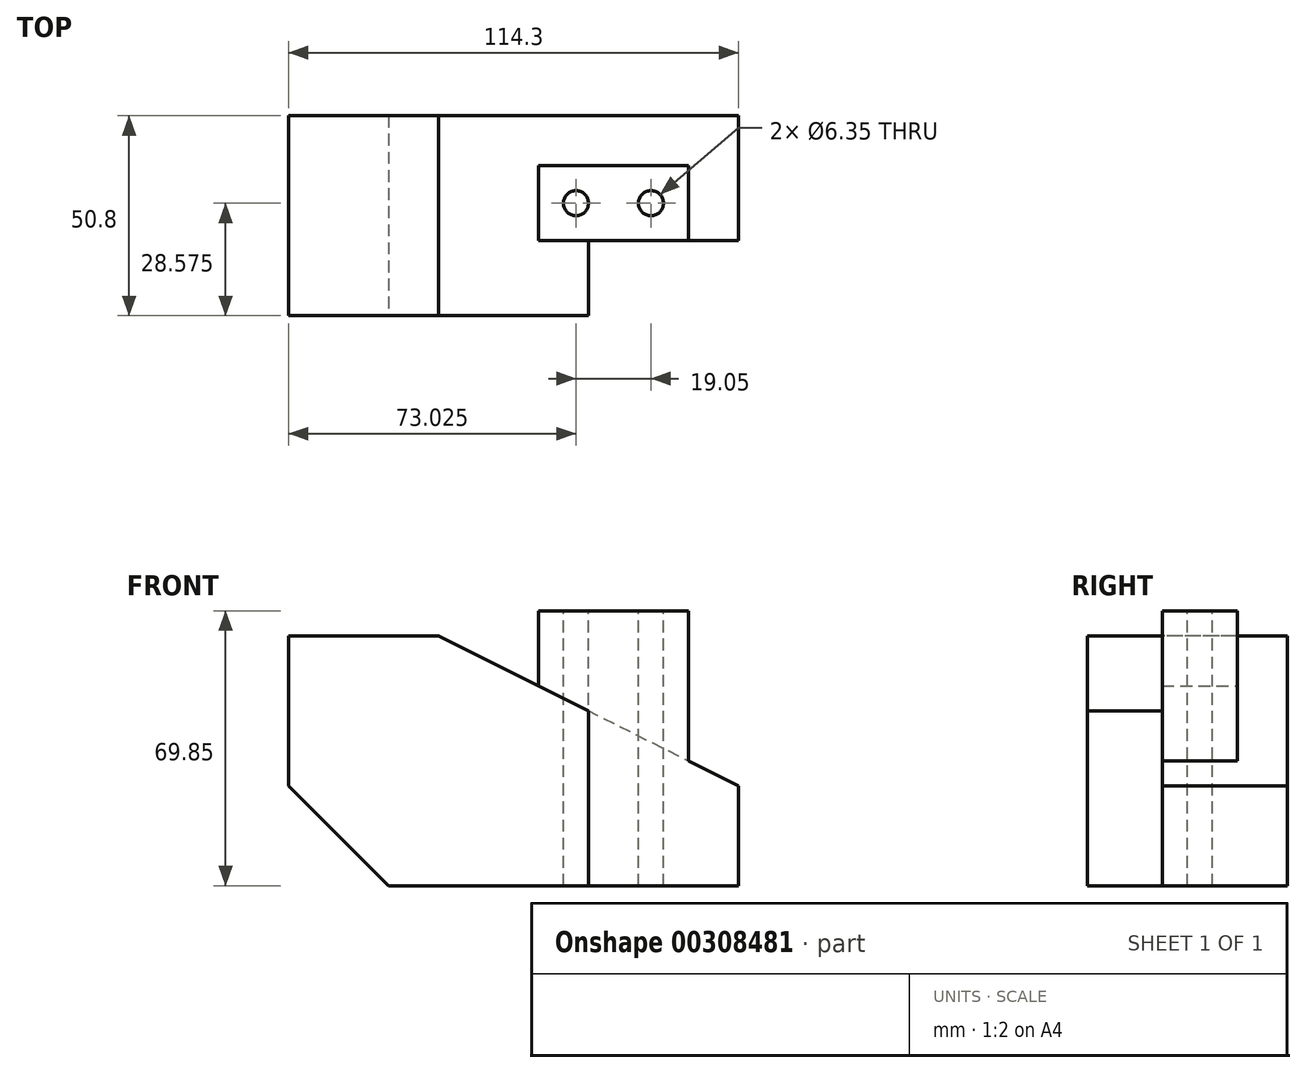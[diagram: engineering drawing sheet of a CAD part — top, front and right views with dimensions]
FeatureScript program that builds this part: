
annotation { "Feature Type Name" : "Feature", "Feature Type Description" : "" }
export const myFeature = defineFeature(function(context is Context, id is Id, definition is map)
    precondition{}
    {
        {
            var Q0;
            Q0=qCreatedBy(makeId("Front.planeOp"),FACE);
            var sketch = newSketch(context, id + "F0", { "sketchPlane" : qUnion([Q0])});
            skLineSegment(sketch, "E0", {"start": v(0, 0) * mm, "end": v(0, 38.1) * mm});
            skLineSegment(sketch, "E1", {"start": v(0, 38.1) * mm, "end": v(38.1, 38.1) * mm});
            skLineSegment(sketch, "E2", {"start": v(38.1, 38.1) * mm, "end": v(76.2, 19.05) * mm});
            skLineSegment(sketch, "E3", {"start": v(25.4, -25.4) * mm, "end": v(0, 0) * mm});
            skLineSegment(sketch, "E4", {"start": v(76.2, 19.05) * mm, "end": v(114.3, 0) * mm});
            skLineSegment(sketch, "E5", {"start": v(114.3, 0) * mm, "end": v(114.3, -25.4) * mm});
            skLineSegment(sketch, "E6", {"start": v(114.3, -25.4) * mm, "end": v(25.4, -25.4) * mm});
            skSolve(sketch);
        }
        {
            var Q0;
            Q0 = qSketchRegion(id + "F0", true);
            extrude(context, id + "F1", {"entities" : qUnion([Q0]), "oppositeDirection" : true, "depth" : 50.8 * mm});
        }
        {
            var Q0;
            Q0=qCreatedBy(makeId("Front.planeOp"),FACE);
            cPlane(context, id + "F2", {"entities" : qUnion([Q0]), "cplaneType" : CPlaneType.OFFSET, "offset" : 19.05 * mm, "oppositeDirection" : true, "width" : 152.4 * mm, "height" : 152.4 * mm});
        }
        {
            var Q0;
            Q0=qCreatedBy(id+"F2.planeOp",FACE);
            var sketch = newSketch(context, id + "F3", { "sketchPlane" : qUnion([Q0])});
            skLineSegment(sketch, "E7", {"start": v(74.02, 6.35) * mm, "end": v(74.02, -25.4) * mm});
            skLineSegment(sketch, "E8", {"start": v(74.02, -25.4) * mm, "end": v(112.12, -25.4) * mm});
            skLineSegment(sketch, "E9", {"start": v(112.12, -25.4) * mm, "end": v(112.12, 0) * mm});
            skLineSegment(sketch, "E10", {"start": v(112.12, 0) * mm, "end": v(99.42, 6.35) * mm});
            skLineSegment(sketch, "E11", {"start": v(74.02, 6.35) * mm, "end": v(99.42, 6.35) * mm});
            skSolve(sketch);
        }
        {
            var Q0;
            Q0 = qSketchRegion(id + "F3", true);
            extrude(context, id + "F4", {"entities" : qUnion([Q0]), "operationType" : NewBodyOperationType.ADD, "oppositeDirection" : true, "depth" : 31.75 * mm});
        }
        {
            var Q0;
            Q0=makeQuery(id+"F1.opExtrude","SWEPT_FACE",FACE,{"disambiguationData":[OSD([sQuery(id+"F0.wireOp",EDGE,"E6")])]});
            var sketch = newSketch(context, id + "F5", { "sketchPlane" : qUnion([Q0])});
            skLineSegment(sketch, "E12", {"start": v(114.3, 0) * mm, "end": v(76.2, 0) * mm});
            skLineSegment(sketch, "E13", {"start": v(76.2, 0) * mm, "end": v(76.2, -19.05) * mm});
            skLineSegment(sketch, "E14", {"start": v(76.2, -19.05) * mm, "end": v(114.3, -19.05) * mm});
            skLineSegment(sketch, "E15", {"start": v(114.3, -19.05) * mm, "end": v(114.3, 0) * mm});
            skSolve(sketch);
        }
        {
            var Q0;
            Q0 = qSketchRegion(id + "F5", true);
            extrude(context, id + "F6", {"entities" : qUnion([Q0]), "operationType" : NewBodyOperationType.REMOVE, "oppositeDirection" : true, "depth" : 101.6 * mm});
        }
        {
            var Q0;
            Q0=makeQuery(id+"F1.opExtrude","SWEPT_FACE",FACE,{"disambiguationData":[OSD([sQuery(id+"F0.wireOp",EDGE,"E6")])]});
            var sketch = newSketch(context, id + "F7", { "sketchPlane" : qUnion([Q0])});
            skLineSegment(sketch, "E16", {"start": v(101.6, -19.05) * mm, "end": v(63.5, -19.05) * mm});
            skLineSegment(sketch, "E17", {"start": v(63.5, -19.05) * mm, "end": v(63.5, -38.1) * mm});
            skLineSegment(sketch, "E18", {"start": v(63.5, -38.1) * mm, "end": v(101.6, -38.1) * mm});
            skLineSegment(sketch, "E19", {"start": v(101.6, -38.1) * mm, "end": v(101.6, -19.05) * mm});
            skSolve(sketch);
        }
        {
            var Q0;
            Q0 = qSketchRegion(id + "F7", true);
            extrude(context, id + "F8", {"entities" : qUnion([Q0]), "operationType" : NewBodyOperationType.ADD, "oppositeDirection" : true, "depth" : 69.85 * mm});
        }
        {
            var Q0;
            Q0=makeQuery(id+"F8.opExtrude","CAP_FACE",FACE,{"disambiguationData":[OSD([sQuery(id+"F7.wireOp",EDGE,"E16"),sQuery(id+"F7.wireOp",EDGE,"E17"),sQuery(id+"F7.wireOp",EDGE,"E18"),sQuery(id+"F7.wireOp",EDGE,"E19")])],"isStart":false});
            var sketch = newSketch(context, id + "F9", { "sketchPlane" : qUnion([Q0])});
            skCircle(sketch, "E20", {"center": v(73.02, 28.57) * mm, "radius": 3.18 * mm});
            skCircle(sketch, "E21", {"center": v(92.07, 28.58) * mm, "radius": 3.18 * mm});
            skSolve(sketch);
        }
        {
            var Q0;
            Q0 = qSketchRegion(id + "F9", true);
            extrude(context, id + "F10", {"entities" : qUnion([Q0]), "operationType" : NewBodyOperationType.REMOVE, "oppositeDirection" : true, "depth" : 69.85 * mm});
        }
    });
